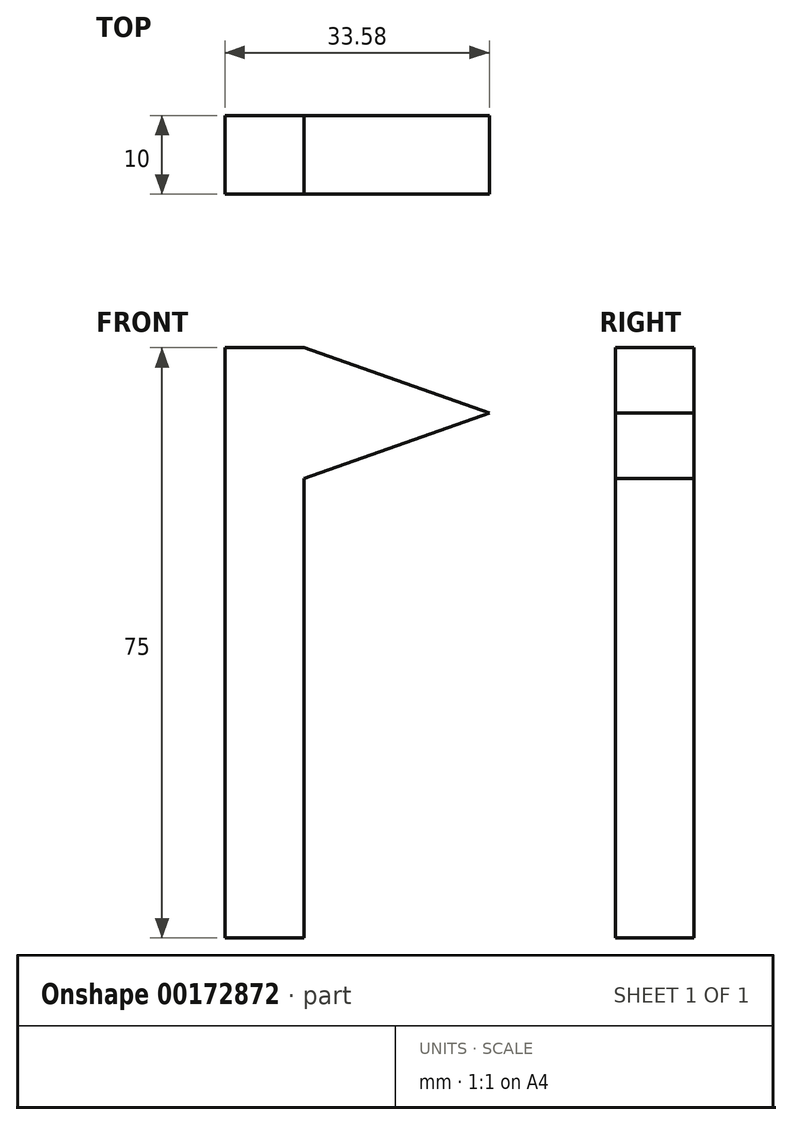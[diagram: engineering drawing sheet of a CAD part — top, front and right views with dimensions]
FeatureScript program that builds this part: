
annotation { "Feature Type Name" : "Feature", "Feature Type Description" : "" }
export const myFeature = defineFeature(function(context is Context, id is Id, definition is map)
    precondition{}
    {
        {
            var Q0;
            Q0=qCreatedBy(makeId("Front.planeOp"),FACE);
            var sketch = newSketch(context, id + "F0", { "sketchPlane" : qUnion([Q0])});
            skLineSegment(sketch, "E0", {"start": v(0, 43.04) * mm, "end": v(-10, 43.04) * mm});
            skLineSegment(sketch, "E1", {"start": v(-10, 43.04) * mm, "end": v(-10, -31.96) * mm});
            skLineSegment(sketch, "E2", {"start": v(-10, -31.96) * mm, "end": v(0, -31.96) * mm});
            skLineSegment(sketch, "E3", {"start": v(0, -31.96) * mm, "end": v(0, 43.04) * mm});
            skLineSegment(sketch, "E4", {"start": v(0, 43.04) * mm, "end": v(23.58, 34.74) * mm});
            skLineSegment(sketch, "E5", {"start": v(23.58, 34.74) * mm, "end": v(0, 26.45) * mm});
            skSolve(sketch);
        }
        {
            var Q0;
            Q0=makeQuery(id+"F0.imprint","IMPRINT",FACE,{"disambiguationData":[TD([[makeQuery(id+"F0.imprint","IMPRINT",EDGE,{"derivedFrom":sQuery(id+"F0.wireOp",EDGE,"E0")}),1.0]])]});
            extrude(context, id + "F1", {"entities" : qUnion([Q0]), "depth" : 10 * mm});
        }
        {
            var Q0;
            Q0 = qSketchRegion(id + "F0", true);
            extrude(context, id + "F2", {"entities" : qUnion([Q0]), "operationType" : NewBodyOperationType.ADD, "depth" : 10 * mm});
        }
    });
